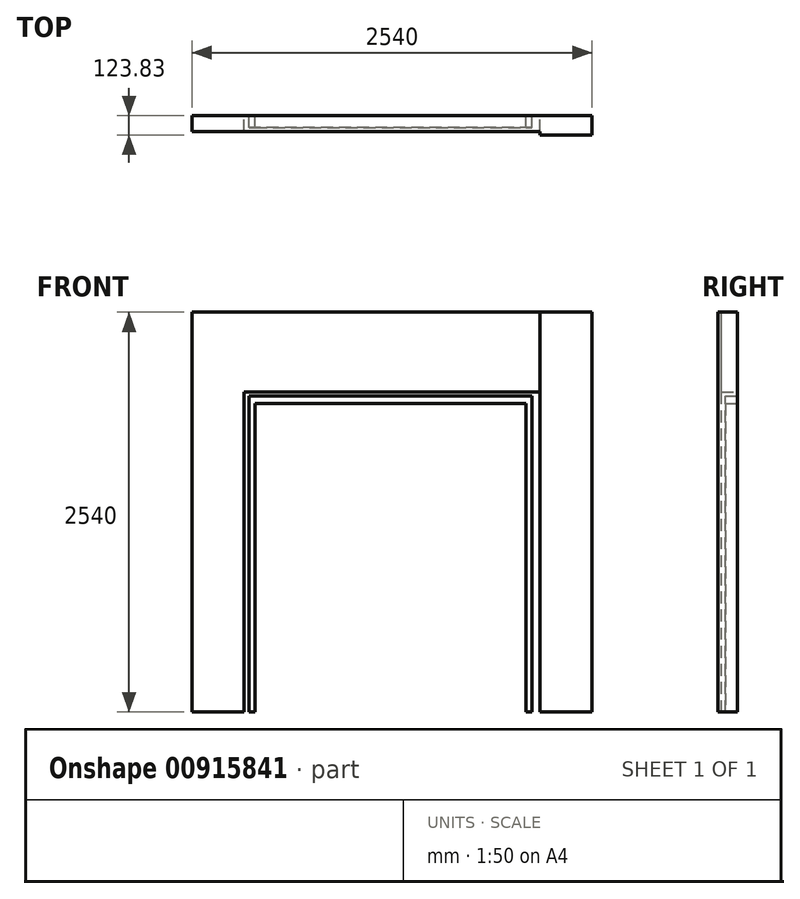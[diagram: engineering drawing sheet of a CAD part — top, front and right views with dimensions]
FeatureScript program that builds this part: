
annotation { "Feature Type Name" : "Feature", "Feature Type Description" : "" }
export const myFeature = defineFeature(function(context is Context, id is Id, definition is map)
    precondition{}
    {
        {
            var Q0;
            Q0=qCreatedBy(makeId("Front.planeOp"),FACE);
            var sketch = newSketch(context, id + "F0", { "sketchPlane" : qUnion([Q0])});
            skLineSegment(sketch, "E0.bottom", {"start": v(0, 0) * mm, "end": v(330.2, 0) * mm});
            skLineSegment(sketch, "E0.top", {"start": v(0, 2540) * mm, "end": v(2540, 2540) * mm});
            skLineSegment(sketch, "E0.left", {"start": v(0, 0) * mm, "end": v(0, 2540) * mm});
            skLineSegment(sketch, "E0.right", {"start": v(2540, 0) * mm, "end": v(2540, 2540) * mm});
            skLineSegment(sketch, "E1.top", {"start": v(330.2, 2032) * mm, "end": v(2209.8, 2032) * mm});
            skLineSegment(sketch, "E1.left", {"start": v(330.2, 0) * mm, "end": v(330.2, 2032) * mm});
            skLineSegment(sketch, "E1.right", {"start": v(2209.8, 0) * mm, "end": v(2209.8, 2032) * mm});
            skLineSegment(sketch, "E2", {"start": v(1270, 2540) * mm, "end": v(1270, 2032) * mm, "construction": true});
            skLineSegment(sketch, "E3.trimOffspring", {"start": v(2209.8, 0) * mm, "end": v(2540, 0) * mm});
            skPoint(sketch, "E4.orphan", {"position": v(1270, 0) * mm});
            skSolve(sketch);
        }
        {
            var Q0;
            Q0=makeQuery(id+"F0.imprint","IMPRINT",FACE,{"disambiguationData":[TD([[makeQuery(id+"F0.imprint","IMPRINT",EDGE,{"derivedFrom":sQuery(id+"F0.wireOp",EDGE,"E0.bottom")}),1.0]])]});
            extrude(context, id + "F1", {"entities" : qUnion([Q0]), "depth" : 101.6 * mm, "offsetDistance" : 25.4 * mm});
        }
        {
            var Q0;
            Q0=makeQuery(id+"F1.opExtrude","CAP_FACE",FACE,{"disambiguationData":[OSD([sQuery(id+"F0.wireOp",EDGE,"E0.bottom"),sQuery(id+"F0.wireOp",EDGE,"E0.top"),sQuery(id+"F0.wireOp",EDGE,"E0.left"),sQuery(id+"F0.wireOp",EDGE,"E0.right"),sQuery(id+"F0.wireOp",EDGE,"E1.top"),sQuery(id+"F0.wireOp",EDGE,"E1.left"),sQuery(id+"F0.wireOp",EDGE,"E1.right"),sQuery(id+"F0.wireOp",EDGE,"E3.trimOffspring")])],"isStart":false});
            var sketch = newSketch(context, id + "F2", { "sketchPlane" : qUnion([Q0])});
            skLineSegment(sketch, "E5.bottom", {"start": v(2209.8, 0) * mm, "end": v(2540, 0) * mm});
            skLineSegment(sketch, "E5.top", {"start": v(2209.8, 2540) * mm, "end": v(2540, 2540) * mm});
            skLineSegment(sketch, "E5.left", {"start": v(2209.8, 0) * mm, "end": v(2209.8, 2540) * mm});
            skLineSegment(sketch, "E5.right", {"start": v(2540, 0) * mm, "end": v(2540, 2540) * mm});
            skSolve(sketch);
        }
        {
            var Q0;
            Q0 = qSketchRegion(id + "F2", true);
            extrude(context, id + "F3", {"entities" : qUnion([Q0]), "operationType" : NewBodyOperationType.ADD, "depth" : 22.22 * mm, "offsetDistance" : 25.4 * mm});
        }
        {
            var Q0;
            Q0=makeQuery(id+"F1.opExtrude","CAP_FACE",FACE,{"disambiguationData":[OSD([sQuery(id+"F0.wireOp",EDGE,"E0.bottom"),sQuery(id+"F0.wireOp",EDGE,"E0.top"),sQuery(id+"F0.wireOp",EDGE,"E0.left"),sQuery(id+"F0.wireOp",EDGE,"E0.right"),sQuery(id+"F0.wireOp",EDGE,"E1.top"),sQuery(id+"F0.wireOp",EDGE,"E1.left"),sQuery(id+"F0.wireOp",EDGE,"E1.right"),sQuery(id+"F0.wireOp",EDGE,"E3.trimOffspring")])],"isStart":true});
            var sketch = newSketch(context, id + "F4", { "sketchPlane" : qUnion([Q0])});
            skLineSegment(sketch, "E6", {"start": v(-1270, 2032) * mm, "end": v(-1270, 0) * mm, "construction": true});
            skLineSegment(sketch, "E7", {"start": v(-2159, 0) * mm, "end": v(-2159, 2006.6) * mm});
            skLineSegment(sketch, "E8", {"start": v(-2159, 2006.6) * mm, "end": v(-361.95, 2006.6) * mm});
            skLineSegment(sketch, "E9", {"start": v(-361.95, 2006.6) * mm, "end": v(-361.95, 0) * mm});
            skLineSegment(sketch, "E10", {"start": v(-361.95, 0) * mm, "end": v(-400.05, 0) * mm});
            skLineSegment(sketch, "E11", {"start": v(-400.05, 0) * mm, "end": v(-400.05, 1958.98) * mm});
            skLineSegment(sketch, "E12", {"start": v(-400.05, 1958.97) * mm, "end": v(-2120.9, 1958.97) * mm});
            skLineSegment(sketch, "E13", {"start": v(-2120.9, 1958.97) * mm, "end": v(-2120.9, 0) * mm});
            skLineSegment(sketch, "E14", {"start": v(-2120.9, 0) * mm, "end": v(-2159, 0) * mm});
            skSolve(sketch);
        }
        {
            var Q0;
            Q0 = qSketchRegion(id + "F4", true);
            extrude(context, id + "F5", {"entities" : qUnion([Q0]), "oppositeDirection" : true, "depth" : 76.2 * mm, "offsetDistance" : 25.4 * mm});
        }
    });
